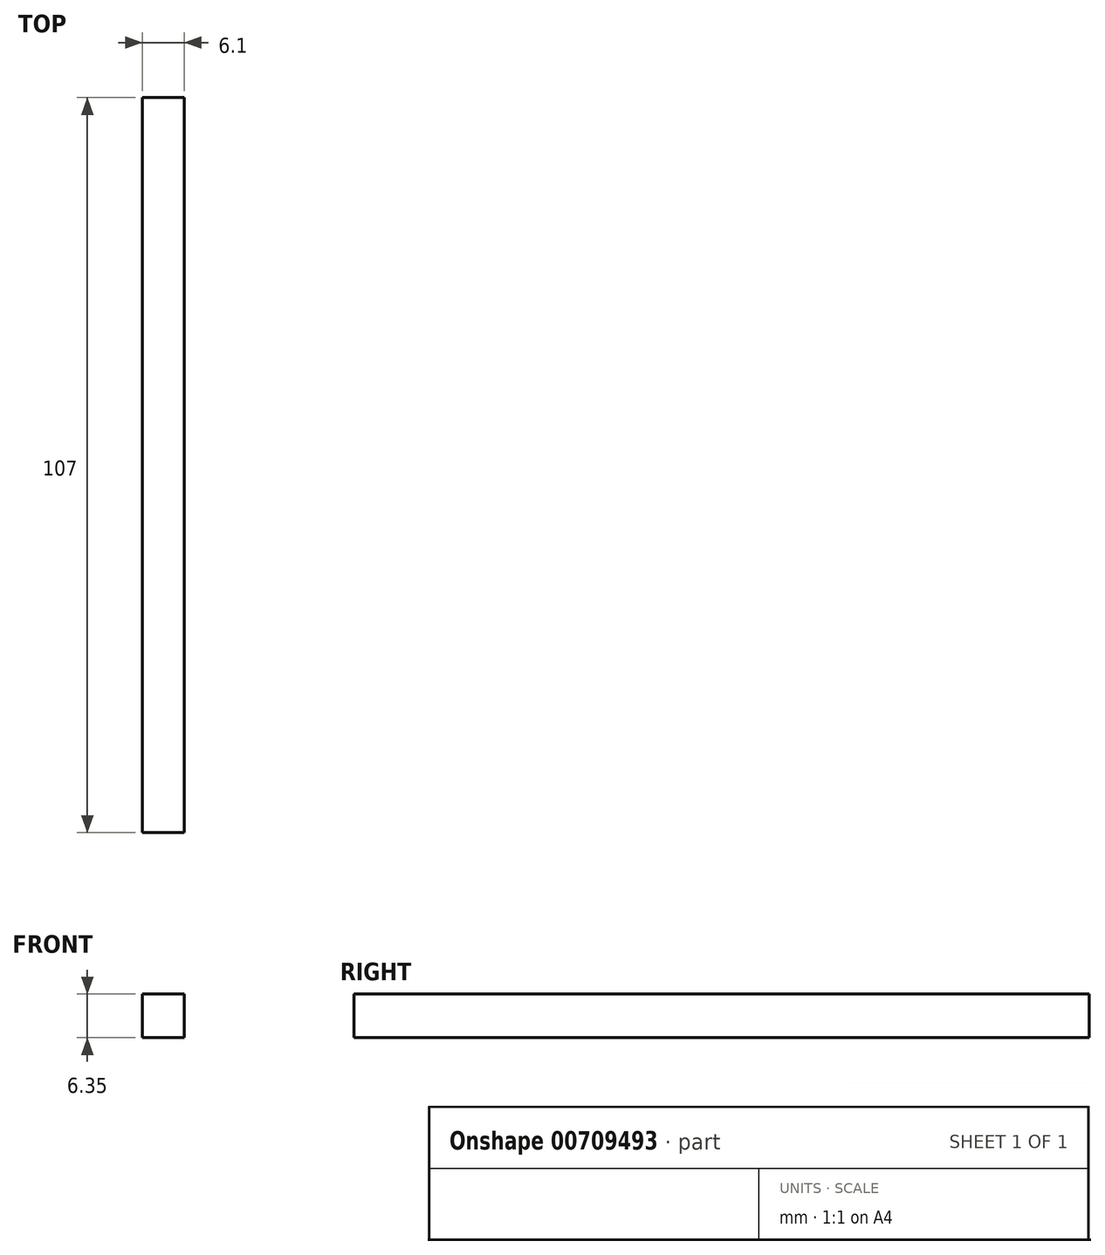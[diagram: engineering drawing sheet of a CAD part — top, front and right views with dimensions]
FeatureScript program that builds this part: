
annotation { "Feature Type Name" : "Feature", "Feature Type Description" : "" }
export const myFeature = defineFeature(function(context is Context, id is Id, definition is map)
    precondition{}
    {
        {
            var Q0;
            Q0=qCreatedBy(makeId("Top.planeOp"),FACE);
            var sketch = newSketch(context, id + "F0", { "sketchPlane" : qUnion([Q0])});
            skLineSegment(sketch, "E0.bottom", {"start": v(0, 0) * mm, "end": v(6.1, 0) * mm});
            skLineSegment(sketch, "E0.top", {"start": v(0, -107) * mm, "end": v(6.1, -107) * mm});
            skLineSegment(sketch, "E0.left", {"start": v(0, 0) * mm, "end": v(0, -107) * mm});
            skLineSegment(sketch, "E0.right", {"start": v(6.1, 0) * mm, "end": v(6.1, -107) * mm});
            skSolve(sketch);
        }
        {
            var Q0;
            Q0=makeQuery(id+"F0.imprint","IMPRINT",FACE,{"disambiguationData":[TD([[makeQuery(id+"F0.imprint","IMPRINT",EDGE,{"derivedFrom":sQuery(id+"F0.wireOp",EDGE,"E0.bottom")}),-1.0]])]});
            extrude(context, id + "F1", {"entities" : qUnion([Q0]), "depth" : 6.35 * mm, "offsetDistance" : 25.4 * mm});
        }
    });
